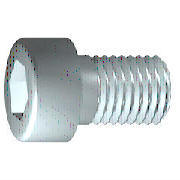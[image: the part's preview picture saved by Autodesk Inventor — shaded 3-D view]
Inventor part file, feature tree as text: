
AUTODESK INVENTOR PART (.ipt)
format: ipt  version: 2021 (Build 250183000, 183)  size: 195,072 bytes
history: native  units: mm (DEFAULTED — no unit token found)
features: other x3, fillet x2, extrude x1, chamfer x1, plane x1
ambient origin geometry x7: Origin, YZ Plane, XY Plane, X Axis, Y Axis, Z Axis, Center Point
bodies: Solid1 (feature_tree)
feature tree (8):
  other  "Corpo"
  extrude  "Fenda"  Depth=8.25mm
  fillet  "Raio de arredondamento1"  Radius=0.429515mm
  chamfer  "Chanfrar1"  Distance=4.0mm
  plane  "Work Plane1"
  fillet  "Fillet2"  Radius=2.0mm
  other  "Rascunho1"
  other  "Rascunho2"
